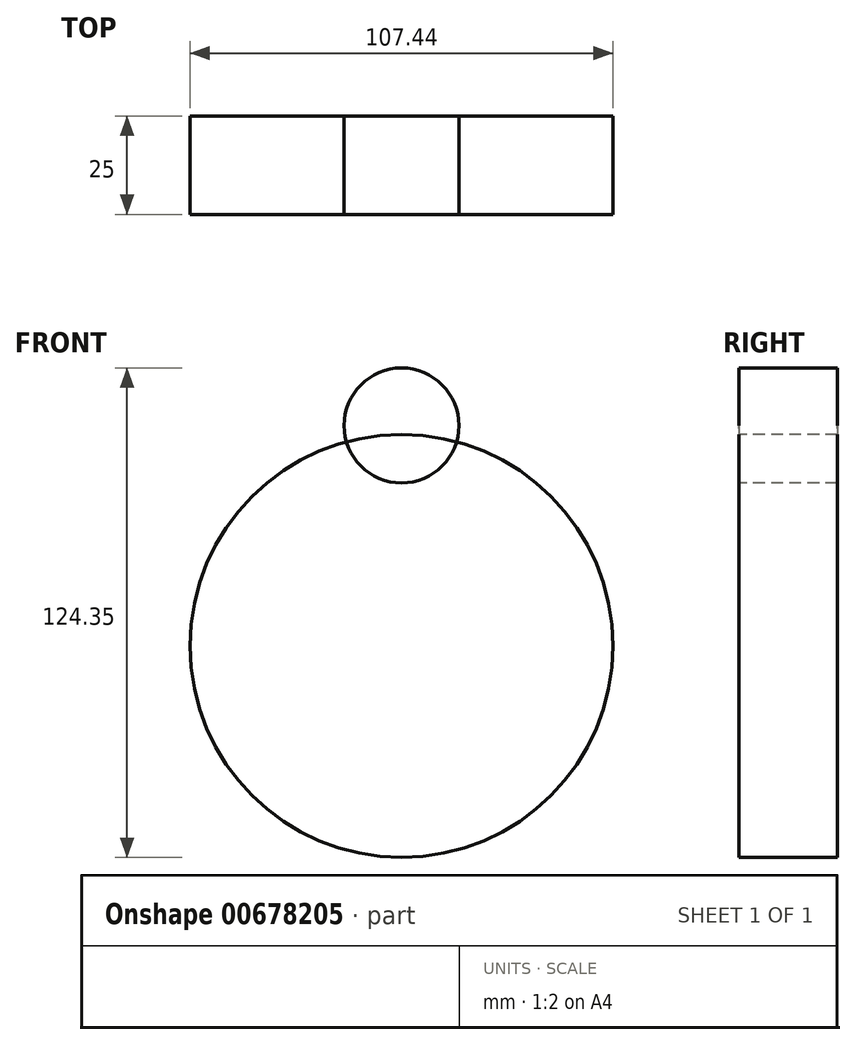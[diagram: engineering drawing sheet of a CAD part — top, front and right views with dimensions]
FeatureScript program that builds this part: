
annotation { "Feature Type Name" : "Feature", "Feature Type Description" : "" }
export const myFeature = defineFeature(function(context is Context, id is Id, definition is map)
    precondition{}
    {
        {
            var Q0;
            Q0=qCreatedBy(makeId("Front.planeOp"),FACE);
            var sketch = newSketch(context, id + "F0", { "sketchPlane" : qUnion([Q0])});
            skCircle(sketch, "E0", {"center": v(0, 0) * mm, "radius": 63.5 * mm, "construction": true});
            skCircle(sketch, "E1", {"center": v(0, 0) * mm, "radius": 58.67 * mm, "construction": true});
            skCircle(sketch, "E2", {"center": v(0, 0) * mm, "radius": 53.72 * mm});
            skLineSegment(sketch, "E3", {"start": v(0, 0) * mm, "end": v(0, 87.56) * mm, "construction": true});
            skLineSegment(sketch, "E4", {"start": v(0, 0) * mm, "end": v(-5.1, 92.78) * mm, "construction": true});
            skLineSegment(sketch, "E5", {"start": v(0, 58.67) * mm, "end": v(-60.6, 58.67) * mm, "construction": true});
            skLineSegment(sketch, "E6", {"start": v(0, 56.03) * mm, "end": v(-58.57, 38.67) * mm, "construction": true});
            skCircle(sketch, "E7", {"center": v(0, 0) * mm, "radius": 53.72 * mm, "construction": true});
            skCircle(sketch, "E8", {"center": v(0, 56.03) * mm, "radius": 14.6 * mm});
            skCircle(sketch, "E9", {"center": v(-14, 51.88) * mm, "radius": 14.6 * mm, "construction": true});
            skArc(sketch, "E10", {"start": v(0, 58.67) * mm, "mid": v(-3.37, 62.17) * mm, "end": v(-7.4, 64.9) * mm});
            skSolve(sketch);
        }
        {
            var Q0;
            Q0=sQuery(id+"F0.wireOp",EDGE,"E8");
            extrude(context, id + "F1", {"bodyType" : ToolBodyType.SURFACE, "surfaceEntities" : qUnion([Q0]), "endBound" : BoundingType.SYMMETRIC, "depth" : 25 * mm, "offsetDistance" : 25 * mm});
        }
        {
            var Q0;
            Q0=sQuery(id+"F0.wireOp",EDGE,"E8");
            extrude(context, id + "F2", {"bodyType" : ToolBodyType.SURFACE, "surfaceEntities" : qUnion([Q0]), "endBound" : BoundingType.SYMMETRIC, "depth" : 25 * mm, "offsetDistance" : 25 * mm});
        }
        {
            var Q0;
            Q0=sQuery(id+"F0.wireOp",EDGE,"E2");
            extrude(context, id + "F3", {"bodyType" : ToolBodyType.SURFACE, "surfaceEntities" : qUnion([Q0]), "endBound" : BoundingType.SYMMETRIC, "depth" : 25 * mm, "offsetDistance" : 25 * mm});
        }
    });
